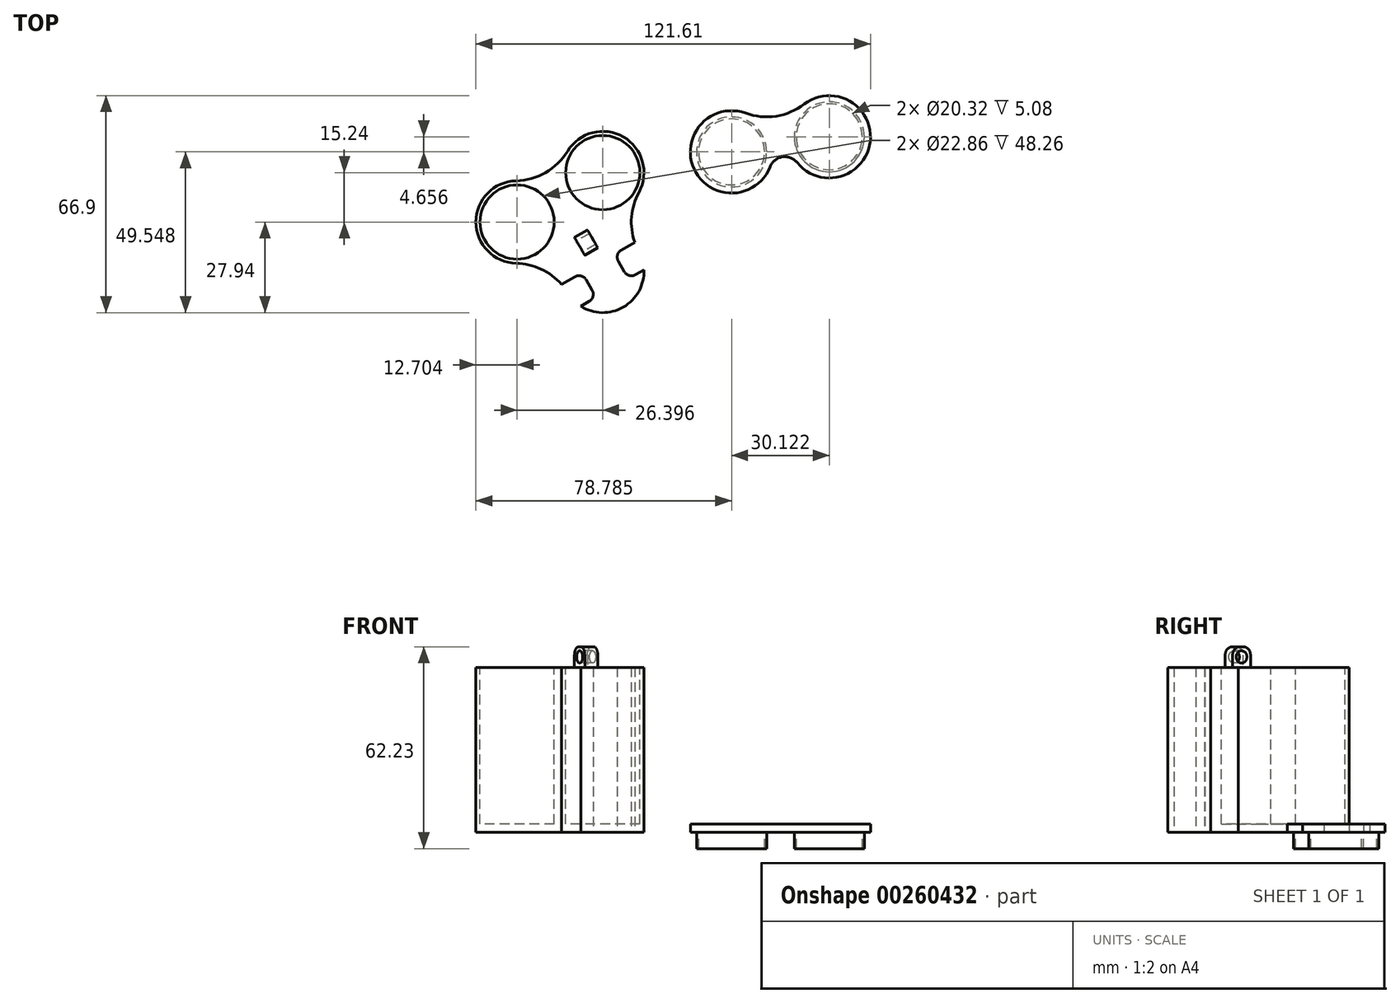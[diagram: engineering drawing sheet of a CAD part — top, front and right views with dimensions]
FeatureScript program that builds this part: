
annotation { "Feature Type Name" : "Feature", "Feature Type Description" : "" }
export const myFeature = defineFeature(function(context is Context, id is Id, definition is map)
    precondition{}
    {
        {
            var Q0;
            Q0=qCreatedBy(makeId("Top.planeOp"),FACE);
            var sketch = newSketch(context, id + "F0", { "sketchPlane" : qUnion([Q0])});
            skCircle(sketch, "E0", {"center": v(-26.4, -15.24) * mm, "radius": 12.7 * mm});
            skCircle(sketch, "E1", {"center": v(0, 0) * mm, "radius": 12.7 * mm});
            skPoint(sketch, "E2", {"position": v(-8.8, -15.24) * mm});
            skCircle(sketch, "E3", {"center": v(-8.8, -15.24) * mm, "radius": 4.9 * mm});
            skArc(sketch, "E4.filletArc", {"start": v(11.14, -6.1) * mm, "mid": v(8.87, -13.65) * mm, "end": v(9.85, -21.48) * mm});
            skArc(sketch, "E5.filletArc", {"start": v(-26.69, -2.54) * mm, "mid": v(-17.6, 0) * mm, "end": v(-10.85, 6.6) * mm});
            skCircle(sketch, "E6", {"center": v(0, 0) * mm, "radius": 11.43 * mm});
            skCircle(sketch, "E7", {"center": v(-26.4, -15.24) * mm, "radius": 11.43 * mm});
            skCircle(sketch, "E8", {"center": v(0, -30.48) * mm, "radius": 5.72 * mm, "construction": true});
            skLineSegment(sketch, "E9", {"start": v(13.71, -28) * mm, "end": v(13.71, -28) * mm});
            skLineSegment(sketch, "E10", {"start": v(-8.8, -15.24) * mm, "end": v(6.35, -41.48) * mm, "construction": true});
            skPoint(sketch, "E11", {"position": v(-12.72, -34.52) * mm});
            skPoint(sketch, "E12", {"position": v(9.85, -21.48) * mm});
            skLineSegment(sketch, "E13", {"start": v(-5.11, -33.06) * mm, "end": v(-3.26, -36.27) * mm});
            skLineSegment(sketch, "E14", {"start": v(4.79, -27.34) * mm, "end": v(6.64, -30.55) * mm});
            skLineSegment(sketch, "E15", {"start": v(-12.72, -34.52) * mm, "end": v(-8.58, -32.13) * mm});
            skLineSegment(sketch, "E16", {"start": v(5.72, -23.87) * mm, "end": v(9.85, -21.48) * mm});
            skLineSegment(sketch, "E17", {"start": v(-6.77, -41.23) * mm, "end": v(-4.19, -39.74) * mm});
            skLineSegment(sketch, "E18", {"start": v(12.7, -30) * mm, "end": v(10.1, -31.48) * mm});
            skArc(sketch, "E19", {"start": v(-12.72, -34.52) * mm, "mid": v(-19, -29.75) * mm, "end": v(-26.69, -27.94) * mm});
            skPoint(sketch, "E20.visualSharp", {"position": v(-6.38, -30.86) * mm});
            skArc(sketch, "E20.filletArc", {"start": v(-5.11, -33.06) * mm, "mid": v(-6.65, -31.87) * mm, "end": v(-8.58, -32.13) * mm});
            skPoint(sketch, "E21.visualSharp", {"position": v(3.52, -25.14) * mm});
            skArc(sketch, "E21.filletArc", {"start": v(5.72, -23.87) * mm, "mid": v(4.53, -25.41) * mm, "end": v(4.79, -27.34) * mm});
            skPoint(sketch, "E22.visualSharp", {"position": v(-1.99, -38.47) * mm});
            skArc(sketch, "E22.filletArc", {"start": v(-4.19, -39.74) * mm, "mid": v(-3, -38.2) * mm, "end": v(-3.26, -36.27) * mm});
            skPoint(sketch, "E23.visualSharp", {"position": v(7.91, -32.75) * mm});
            skArc(sketch, "E23.filletArc", {"start": v(6.64, -30.55) * mm, "mid": v(8.18, -31.73) * mm, "end": v(10.1, -31.48) * mm});
            skArc(sketch, "E24", {"start": v(-12.15, -34.18) * mm, "mid": v(-10.1, -38.19) * mm, "end": v(-6.77, -41.23) * mm, "construction": true});
            skArc(sketch, "E25", {"start": v(9.28, -21.81) * mm, "mid": v(-6.35, -19.48) * mm, "end": v(-12.15, -34.18) * mm});
            skArc(sketch, "E26", {"start": v(12.7, -30) * mm, "mid": v(11.72, -25.6) * mm, "end": v(9.28, -21.81) * mm, "construction": true});
            skArc(sketch, "E27", {"start": v(-6.77, -41.23) * mm, "mid": v(6.35, -41.48) * mm, "end": v(12.7, -30) * mm});
            skSolve(sketch);
        }
        {
            var Q0;
            Q0=makeQuery(id+"F0.imprint","IMPRINT",FACE,{"disambiguationData":[TD([[makeQuery(id+"F0.imprint","IMPRINT",EDGE,{"derivedFrom":sQuery(id+"F0.wireOp",EDGE,"aVx5bCA9-Pl4H-8Tk4-ZB0N-MlAAreGqP8em")}),-1.0]])]});
            var Q1;
            {var subQ0=sQuery(id+"F0.wireOp",EDGE,"d5061103-f5dd-4c88-93f0-6c43c21c0ec2.filletArc");Q1=makeQuery(id+"F0.imprint","IMPRINT",FACE,{"disambiguationData":[TD([[makeQuery(id+"F0.imprint","IMPRINT",EDGE,{"derivedFrom":subQ0}),-1.0]])]});}
            var Q2;
            {var subQ0=sQuery(id+"F0.wireOp",EDGE,"E4.filletArc");Q2=makeQuery(id+"F0.imprint","IMPRINT",FACE,{"disambiguationData":[TD([[makeQuery(id+"F0.imprint","IMPRINT",EDGE,{"derivedFrom":subQ0}),-1.0]])]});}
            var Q3;
            {var subQ0=sQuery(id+"F0.wireOp",EDGE,"E5.filletArc");Q3=makeQuery(id+"F0.imprint","IMPRINT",FACE,{"disambiguationData":[TD([[makeQuery(id+"F0.imprint","IMPRINT",EDGE,{"derivedFrom":subQ0}),-1.0]])]});}
            var Q4;
            Q4=makeQuery(id+"F0.imprint","IMPRINT",FACE,{"disambiguationData":[TD([[makeQuery(id+"F0.imprint","IMPRINT",EDGE,{"derivedFrom":sQuery(id+"F0.wireOp",EDGE,"E6")}),-1.0]])]});
            var Q5;
            Q5=makeQuery(id+"F0.imprint","IMPRINT",FACE,{"disambiguationData":[TD([[makeQuery(id+"F0.imprint","IMPRINT",EDGE,{"derivedFrom":sQuery(id+"F0.wireOp",EDGE,"E7")}),-1.0]])]});
            var Q6;
            {var subQ0=sQuery(id+"F0.wireOp",EDGE,"E3");var subQ1=sQuery(id+"F0.wireOp",EDGE,"E0");var subQ2=makeQuery(id+"F0.imprint","INTERSECT",VERTEX,{"disambiguationData":[OD(1.0)],"derivedFrom":[subQ1,subQ0]});Q6=makeQuery(id+"F0.imprint","IMPRINT",FACE,{"disambiguationData":[TD([[makeQuery(id+"F0.imprint","IMPRINT",EDGE,{"disambiguationData":[TD([[subQ2,1.0]])],"derivedFrom":subQ0}),1.0]])]});}
            var Q7;
            Q7=makeQuery(id+"F0.imprint","IMPRINT",FACE,{"disambiguationData":[TD([[makeQuery(id+"F0.imprint","IMPRINT",EDGE,{"derivedFrom":sQuery(id+"F0.wireOp",EDGE,"E7")}),1.0]])]});
            var Q8;
            Q8=makeQuery(id+"F0.imprint","IMPRINT",FACE,{"disambiguationData":[TD([[makeQuery(id+"F0.imprint","IMPRINT",EDGE,{"derivedFrom":sQuery(id+"F0.wireOp",EDGE,"E6")}),1.0]])]});
            var Q9;
            {var subQ7=sQuery(id+"F0.wireOp",EDGE,"E19");Q9=makeQuery(id+"F0.imprint","IMPRINT",FACE,{"disambiguationData":[TD([[makeQuery(id+"F0.imprint","IMPRINT",EDGE,{"derivedFrom":subQ7}),-1.0]])]});}
            var Q10;
            Q10=makeQuery(id+"F0.imprint","IMPRINT",FACE,{"disambiguationData":[TD([[makeQuery(id+"F0.imprint","IMPRINT",EDGE,{"derivedFrom":sQuery(id+"F0.wireOp",EDGE,"E13")}),1.0]])]});
            extrude(context, id + "F1", {"entities" : qUnion([Q0, Q1, Q2, Q3, Q4, Q5, Q6, Q7, Q8, Q9, Q10]), "depth" : 50.8 * mm});
        }
        {
            var Q0;
            Q0=makeQuery(id+"F1.opExtrude","CAP_FACE",FACE,{"disambiguationData":[OSD([sQuery(id+"F0.wireOp",EDGE,"E0"),sQuery(id+"F0.wireOp",EDGE,"E1"),sQuery(id+"F0.wireOp",EDGE,"d5061103-f5dd-4c88-93f0-6c43c21c0ec2.filletArc"),sQuery(id+"F0.wireOp",EDGE,"E4.filletArc"),sQuery(id+"F0.wireOp",EDGE,"E5.filletArc"),sQuery(id+"F0.wireOp",EDGE,"aVx5bCA9-Pl4H-8Tk4-ZB0N-MlAAreGqP8em"),sQuery(id+"F0.wireOp",EDGE,"swpA4COB-LIlp-gCge-2OUZ-TmKzK8ej3zXg"),sQuery(id+"F0.wireOp",EDGE,"wXpBnsDd-V7pK-W9gH-srih-m6Xv3qnmRDf4"),sQuery(id+"F0.wireOp",EDGE,"7aa9a101-78a8-4a2e-ba88-899015d45353.filletArc"),sQuery(id+"F0.wireOp",EDGE,"0CHuUY8a-V8Xz-yseA-bI2k-vIzbX0agHWlY"),sQuery(id+"F0.wireOp",EDGE,"2858c310-cecc-49e7-9145-291fe06b1c72.filletArc"),sQuery(id+"F0.wireOp",EDGE,"2e4f5714-7d4d-4278-9bef-307c80793631.filletArc"),sQuery(id+"F0.wireOp",EDGE,"vva0f9Bb-g2Ri-s7oT-Wjy6-6m2MaTEuv8a6"),sQuery(id+"F0.wireOp",EDGE,"30137454-808b-4b01-9027-f336ffe45562.filletArc"),sQuery(id+"F0.wireOp",EDGE,"9274c2ac-97c9-46b1-90ad-2fabd2dcc2cd"),sQuery(id+"F0.wireOp",EDGE,"15f4eca0-4227-403e-addc-07e354998ee51"),sQuery(id+"F0.wireOp",EDGE,"0b93a303-fd0d-48ff-a5ba-763926771dc6"),sQuery(id+"F0.wireOp",EDGE,"9077dd2d-1ab5-4fb2-8ae4-ef6a03d265e3")])],"isStart":false});
            var sketch = newSketch(context, id + "F2", { "sketchPlane" : qUnion([Q0])});
            skCircle(sketch, "E28", {"center": v(0, 0) * mm, "radius": 11.43 * mm});
            skCircle(sketch, "E29", {"center": v(-26.4, -15.24) * mm, "radius": 11.43 * mm});
            skSolve(sketch);
        }
        {
            var Q0;
            Q0 = qSketchRegion(id + "F2", true);
            extrude(context, id + "F3", {"entities" : qUnion([Q0]), "operationType" : NewBodyOperationType.REMOVE, "oppositeDirection" : true, "depth" : 48.26 * mm});
        }
        {
            var Q0;
            Q0=makeQuery(id+"F1.opExtrude","CAP_FACE",FACE,{"disambiguationData":[OSD([sQuery(id+"F0.wireOp",EDGE,"E0"),sQuery(id+"F0.wireOp",EDGE,"E1"),sQuery(id+"F0.wireOp",EDGE,"d5061103-f5dd-4c88-93f0-6c43c21c0ec2.filletArc"),sQuery(id+"F0.wireOp",EDGE,"E4.filletArc"),sQuery(id+"F0.wireOp",EDGE,"E5.filletArc"),sQuery(id+"F0.wireOp",EDGE,"E6"),sQuery(id+"F0.wireOp",EDGE,"E7"),sQuery(id+"F0.wireOp",EDGE,"aVx5bCA9-Pl4H-8Tk4-ZB0N-MlAAreGqP8em"),sQuery(id+"F0.wireOp",EDGE,"swpA4COB-LIlp-gCge-2OUZ-TmKzK8ej3zXg"),sQuery(id+"F0.wireOp",EDGE,"wXpBnsDd-V7pK-W9gH-srih-m6Xv3qnmRDf4"),sQuery(id+"F0.wireOp",EDGE,"7aa9a101-78a8-4a2e-ba88-899015d45353.filletArc"),sQuery(id+"F0.wireOp",EDGE,"0CHuUY8a-V8Xz-yseA-bI2k-vIzbX0agHWlY"),sQuery(id+"F0.wireOp",EDGE,"2858c310-cecc-49e7-9145-291fe06b1c72.filletArc"),sQuery(id+"F0.wireOp",EDGE,"2e4f5714-7d4d-4278-9bef-307c80793631.filletArc"),sQuery(id+"F0.wireOp",EDGE,"vva0f9Bb-g2Ri-s7oT-Wjy6-6m2MaTEuv8a6"),sQuery(id+"F0.wireOp",EDGE,"30137454-808b-4b01-9027-f336ffe45562.filletArc"),sQuery(id+"F0.wireOp",EDGE,"9274c2ac-97c9-46b1-90ad-2fabd2dcc2cd"),sQuery(id+"F0.wireOp",EDGE,"15f4eca0-4227-403e-addc-07e354998ee51"),sQuery(id+"F0.wireOp",EDGE,"0b93a303-fd0d-48ff-a5ba-763926771dc6"),sQuery(id+"F0.wireOp",EDGE,"9077dd2d-1ab5-4fb2-8ae4-ef6a03d265e3")])],"isStart":false});
            var sketch = newSketch(context, id + "F4", { "sketchPlane" : qUnion([Q0])});
            skLineSegment(sketch, "E30", {"start": v(-8.71, -20) * mm, "end": v(-4.72, -17.7) * mm});
            skLineSegment(sketch, "E31", {"start": v(-16.68, 3.01) * mm, "end": v(-4.72, -17.7) * mm, "construction": true});
            skLineSegment(sketch, "E32", {"start": v(-1.54, -23.2) * mm, "end": v(-5.53, -25.5) * mm});
            skLineSegment(sketch, "E33", {"start": v(-5.53, -25.5) * mm, "end": v(-8.71, -20) * mm});
            skLineSegment(sketch, "E34", {"start": v(-4.72, -17.7) * mm, "end": v(-1.54, -23.2) * mm});
            skLineSegment(sketch, "E35", {"start": v(-8.71, -20) * mm, "end": v(-21.92, 2.87) * mm, "construction": true});
            skLineSegment(sketch, "E36", {"start": v(-15.63, -11.41) * mm, "end": v(-14.16, -10.56) * mm, "construction": true});
            skLineSegment(sketch, "E37", {"start": v(-14.16, -10.56) * mm, "end": v(-10.17, -8.26) * mm, "construction": true});
            skLineSegment(sketch, "E38", {"start": v(-10.17, -8.26) * mm, "end": v(-8.7, -7.41) * mm, "construction": true});
            skSolve(sketch);
        }
        {
            var Q0;
            Q0=makeQuery(id+"F4.imprint","IMPRINT",FACE,{"disambiguationData":[TD([[makeQuery(id+"F4.imprint","IMPRINT",EDGE,{"derivedFrom":sQuery(id+"F4.wireOp",EDGE,"2mI1C6iC-MgGc-ayft-MGMf-AZWzZydZj245.bottom")}),-1.0]])]});
            var Q1;
            Q1=makeQuery(id+"F4.imprint","IMPRINT",FACE,{"disambiguationData":[TD([[makeQuery(id+"F4.imprint","IMPRINT",EDGE,{"derivedFrom":sQuery(id+"F4.wireOp",EDGE,"E30")}),-1.0]])]});
            extrude(context, id + "F5", {"entities" : qUnion([Q0, Q1]), "operationType" : NewBodyOperationType.ADD, "depth" : 6.35 * mm});
        }
        {
            var Q0;
            Q0=qCreatedBy(makeId("Top.planeOp"),FACE);
            var sketch = newSketch(context, id + "F6", { "sketchPlane" : qUnion([Q0])});
            skCircle(sketch, "E39", {"center": v(39.69, 6.37) * mm, "radius": 12.7 * mm});
            skCircle(sketch, "E40", {"center": v(39.69, 6.37) * mm, "radius": 11.3 * mm});
            skCircle(sketch, "E41", {"center": v(69.8, 11.02) * mm, "radius": 12.7 * mm});
            skCircle(sketch, "E42", {"center": v(69.8, 11.02) * mm, "radius": 11.3 * mm});
            skLineSegment(sketch, "E43", {"start": v(69.8, 11.02) * mm, "end": v(39.69, 6.37) * mm, "construction": true});
            skArc(sketch, "E44.filletArc", {"start": v(44, 18.3) * mm, "mid": v(53.4, 17.4) * mm, "end": v(62.08, 21.1) * mm});
            skCircle(sketch, "E45", {"center": v(56.1, 0) * mm, "radius": 3.81 * mm, "construction": true});
            skArc(sketch, "E46", {"start": v(59.9, 3.07) * mm, "mid": v(55.34, 4.84) * mm, "end": v(51.52, 1.77) * mm});
            skSolve(sketch);
        }
        {
            var Q0;
            {var subQ0=sQuery(id+"F6.wireOp",EDGE,"E44.filletArc");Q0=makeQuery(id+"F6.imprint","IMPRINT",FACE,{"disambiguationData":[TD([[makeQuery(id+"F6.imprint","IMPRINT",EDGE,{"derivedFrom":subQ0}),-1.0]])]});}
            var Q1;
            Q1=makeQuery(id+"F6.imprint","IMPRINT",FACE,{"disambiguationData":[TD([[makeQuery(id+"F6.imprint","IMPRINT",EDGE,{"derivedFrom":sQuery(id+"F6.wireOp",EDGE,"E40")}),-1.0]])]});
            var Q2;
            Q2=makeQuery(id+"F6.imprint","IMPRINT",FACE,{"disambiguationData":[TD([[makeQuery(id+"F6.imprint","IMPRINT",EDGE,{"derivedFrom":sQuery(id+"F6.wireOp",EDGE,"E40")}),1.0]])]});
            var Q3;
            Q3=makeQuery(id+"F6.imprint","IMPRINT",FACE,{"disambiguationData":[TD([[makeQuery(id+"F6.imprint","IMPRINT",EDGE,{"derivedFrom":sQuery(id+"F6.wireOp",EDGE,"E42")}),-1.0]])]});
            var Q4;
            Q4=makeQuery(id+"F6.imprint","IMPRINT",FACE,{"disambiguationData":[TD([[makeQuery(id+"F6.imprint","IMPRINT",EDGE,{"derivedFrom":sQuery(id+"F6.wireOp",EDGE,"E42")}),1.0]])]});
            extrude(context, id + "F7", {"entities" : qUnion([Q0, Q1, Q2, Q3, Q4]), "depth" : 2.54 * mm});
        }
        {
            var Q0;
            Q0=makeQuery(id+"F7.opExtrude","CAP_FACE",FACE,{"disambiguationData":[OSD([sQuery(id+"F6.wireOp",EDGE,"E39"),sQuery(id+"F6.wireOp",EDGE,"E41"),sQuery(id+"F6.wireOp",EDGE,"E44.filletArc"),sQuery(id+"F6.wireOp",EDGE,"E46")])],"isStart":true});
            var sketch = newSketch(context, id + "F8", { "sketchPlane" : qUnion([Q0])});
            skCircle(sketch, "E47", {"center": v(39.69, -6.37) * mm, "radius": 10.8 * mm});
            skCircle(sketch, "E48", {"center": v(39.69, -6.37) * mm, "radius": 10.16 * mm});
            skCircle(sketch, "E49", {"center": v(69.8, -11.02) * mm, "radius": 10.8 * mm});
            skCircle(sketch, "E50", {"center": v(69.8, -11.02) * mm, "radius": 10.16 * mm});
            skSolve(sketch);
        }
        {
            var Q0;
            Q0=makeQuery(id+"F8.imprint","IMPRINT",FACE,{"disambiguationData":[TD([[makeQuery(id+"F8.imprint","IMPRINT",EDGE,{"derivedFrom":sQuery(id+"F8.wireOp",EDGE,"E47")}),1.0]])]});
            var Q1;
            Q1=makeQuery(id+"F8.imprint","IMPRINT",FACE,{"disambiguationData":[TD([[makeQuery(id+"F8.imprint","IMPRINT",EDGE,{"derivedFrom":sQuery(id+"F8.wireOp",EDGE,"E49")}),1.0]])]});
            extrude(context, id + "F9", {"entities" : qUnion([Q0, Q1]), "operationType" : NewBodyOperationType.ADD, "depth" : 5.08 * mm});
        }
        {
            var Q0;
            Q0=makeQuery(id+"F5.opExtrude","CAP_EDGE",EDGE,{"disambiguationData":[OSD([sQuery(id+"F4.wireOp",EDGE,"E32")])],"isStart":false});
            var Q1;
            Q1=makeQuery(id+"F5.opExtrude","CAP_EDGE",EDGE,{"disambiguationData":[OSD([sQuery(id+"F4.wireOp",EDGE,"E30")])],"isStart":false});
            fillet(context, id + "F10", {"entities" : qUnion([Q0, Q1]), "radius" : 2.54 * mm, "tangentPropagation" : true, "allowEdgeOverflow" : false});
        }
        {
            var Q0;
            Q0=makeQuery(id+"F5.opExtrude","SWEPT_FACE",FACE,{"disambiguationData":[OSD([sQuery(id+"F4.wireOp",EDGE,"E33")])]});
            var sketch = newSketch(context, id + "F11", { "sketchPlane" : qUnion([Q0])});
            skPoint(sketch, "E51.centerSnap0", {"position": v(16.14, 57.15) * mm});
            skPoint(sketch, "E52", {"position": v(16.14, 54) * mm});
            skSolve(sketch);
        }
        {
            var Q0;
            Q0=sQuery(id+"F11.wireOp",VERTEX,"E52");
            var Q1;
            Q1=makeQuery(id+"F1.opExtrude","SWEPT_BODY",BODY,{"disambiguationData":[OSD([sQuery(id+"F0.wireOp",EDGE,"E0"),sQuery(id+"F0.wireOp",EDGE,"E1"),sQuery(id+"F0.wireOp",EDGE,"E4.filletArc"),sQuery(id+"F0.wireOp",EDGE,"E5.filletArc"),sQuery(id+"F0.wireOp",EDGE,"E13"),sQuery(id+"F0.wireOp",EDGE,"E14"),sQuery(id+"F0.wireOp",EDGE,"E15"),sQuery(id+"F0.wireOp",EDGE,"E16"),sQuery(id+"F0.wireOp",EDGE,"E17"),sQuery(id+"F0.wireOp",EDGE,"E18"),sQuery(id+"F0.wireOp",EDGE,"adf0e24c-d359-46cf-b362-f2290c63d83c2"),sQuery(id+"F0.wireOp",EDGE,"E19"),sQuery(id+"F0.wireOp",EDGE,"E20.filletArc"),sQuery(id+"F0.wireOp",EDGE,"E21.filletArc"),sQuery(id+"F0.wireOp",EDGE,"E22.filletArc"),sQuery(id+"F0.wireOp",EDGE,"E23.filletArc")])]});
            hole(context, id + "F12", {"style" : HoleStyle.SIMPLE, "endStyle" : HoleEndStyle.THROUGH, "holeDiameter" : 3.8 * mm, "tappedDepth" : 12.7 * mm, "tapClearance" : 3, "locations" : qUnion([Q0]), "scope" : qUnion([Q1])});
        }
    });
